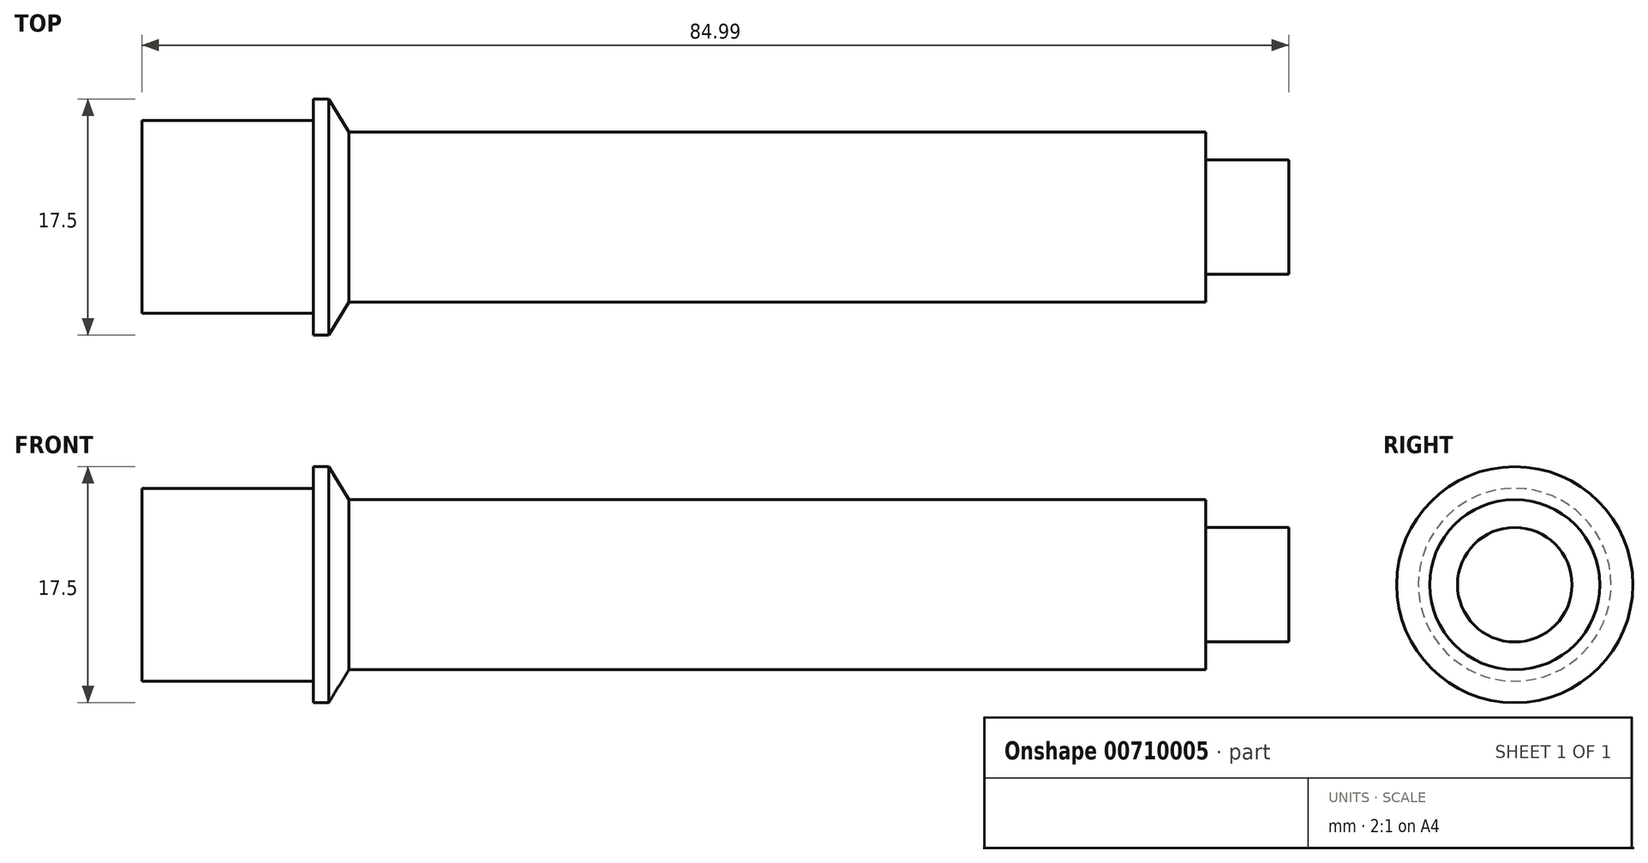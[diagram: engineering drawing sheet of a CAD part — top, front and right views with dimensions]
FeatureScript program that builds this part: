
annotation { "Feature Type Name" : "Feature", "Feature Type Description" : "" }
export const myFeature = defineFeature(function(context is Context, id is Id, definition is map)
    precondition{}
    {
        {
            var Q0;
            Q0=qCreatedBy(makeId("Front.planeOp"),FACE);
            var sketch = newSketch(context, id + "F0", { "sketchPlane" : qUnion([Q0])});
            skLineSegment(sketch, "E0", {"start": v(0, 0) * mm, "end": v(0, 7.14) * mm});
            skLineSegment(sketch, "E1", {"start": v(0, 7.14) * mm, "end": v(12.7, 7.14) * mm});
            skLineSegment(sketch, "E2", {"start": v(12.7, 7.14) * mm, "end": v(12.7, 8.75) * mm});
            skLineSegment(sketch, "E3", {"start": v(12.7, 8.75) * mm, "end": v(13.83, 8.75) * mm});
            skLineSegment(sketch, "E4", {"start": v(13.83, 8.75) * mm, "end": v(15.35, 6.3) * mm});
            skLineSegment(sketch, "E5", {"start": v(15.35, 6.3) * mm, "end": v(78.85, 6.3) * mm});
            skLineSegment(sketch, "E6", {"start": v(78.85, 6.3) * mm, "end": v(78.85, 4.25) * mm});
            skLineSegment(sketch, "E7", {"start": v(78.85, 4.25) * mm, "end": v(84.99, 4.25) * mm});
            skLineSegment(sketch, "E8", {"start": v(84.99, 4.25) * mm, "end": v(84.99, 0) * mm});
            skLineSegment(sketch, "E9", {"start": v(84.99, 0) * mm, "end": v(0, 0) * mm});
            skSolve(sketch);
        }
        {
            var Q0;
            Q0=makeQuery(id+"F0.imprint","IMPRINT",FACE,{"disambiguationData":[TD([[makeQuery(id+"F0.imprint","IMPRINT",EDGE,{"derivedFrom":sQuery(id+"F0.wireOp",EDGE,"E0")}),-1.0]])]});
            var Q1;
            Q1=sQuery(id+"F0.wireOp",EDGE,"E9");
            revolve(context, id + "F1", {"surfaceOperationType" : NewSurfaceOperationType.NEW, "entities" : qUnion([Q0]), "axis" : qUnion([Q1]), "revolveType" : RevolveType.FULL});
        }
    });
